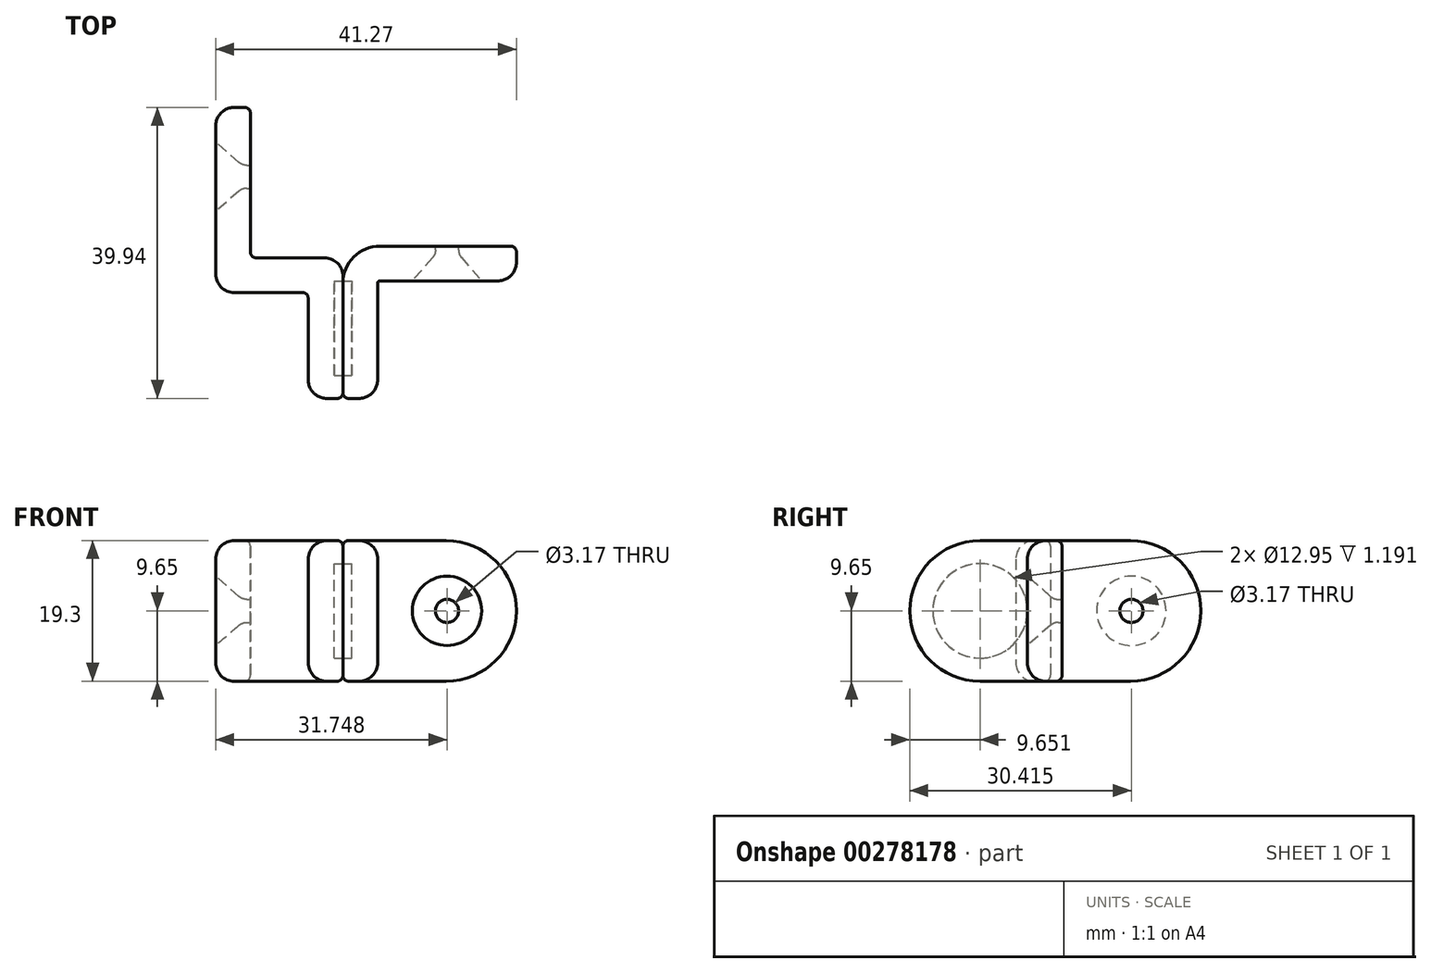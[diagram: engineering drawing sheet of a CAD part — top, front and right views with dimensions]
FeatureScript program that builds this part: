
annotation { "Feature Type Name" : "Feature", "Feature Type Description" : "" }
export const myFeature = defineFeature(function(context is Context, id is Id, definition is map)
    precondition{}
    {
        {
            var Q0;
            Q0=qCreatedBy(makeId("Top.planeOp"),FACE);
            var sketch = newSketch(context, id + "F0", { "sketchPlane" : qUnion([Q0])});
            skLineSegment(sketch, "E0", {"start": v(0, 61) * mm, "end": v(0, 0) * mm, "construction": true});
            skLineSegment(sketch, "E1", {"start": v(0, 0) * mm, "end": v(86.68, 0) * mm, "construction": true});
            skLineSegment(sketch, "E2", {"start": v(0, 19.05) * mm, "end": v(0, -1.59) * mm});
            skLineSegment(sketch, "E3", {"start": v(0, 19.05) * mm, "end": v(-4.76, 19.05) * mm});
            skLineSegment(sketch, "E4", {"start": v(-4.76, 19.05) * mm, "end": v(-4.76, -6.35) * mm});
            skLineSegment(sketch, "E5", {"start": v(0, -1.59) * mm, "end": v(12.7, -1.59) * mm});
            skLineSegment(sketch, "E6", {"start": v(12.7, -1.59) * mm, "end": v(12.7, -20.9) * mm});
            skLineSegment(sketch, "E7", {"start": v(12.7, -20.9) * mm, "end": v(7.94, -20.9) * mm});
            skLineSegment(sketch, "E8", {"start": v(12.7, -4.76) * mm, "end": v(11.5, -4.76) * mm, "construction": true});
            skLineSegment(sketch, "E9", {"start": v(11.5, -4.76) * mm, "end": v(11.5, -17.72) * mm, "construction": true});
            skLineSegment(sketch, "E10", {"start": v(11.5, -17.72) * mm, "end": v(12.7, -17.72) * mm, "construction": true});
            skLineSegment(sketch, "E11", {"start": v(12.7, -11.24) * mm, "end": v(26.67, -11.24) * mm, "construction": true});
            skLineSegment(sketch, "E12", {"start": v(-4.76, 9.53) * mm, "end": v(13.54, 9.53) * mm, "construction": true});
            skLineSegment(sketch, "E13", {"start": v(-4.76, -6.35) * mm, "end": v(7.94, -6.35) * mm});
            skLineSegment(sketch, "E14", {"start": v(7.94, -6.35) * mm, "end": v(7.94, -20.9) * mm});
            skSolve(sketch);
        }
        {
            var Q0;
            Q0=qCreatedBy(makeId("Top.planeOp"),FACE);
            var sketch = newSketch(context, id + "F1", { "sketchPlane" : qUnion([Q0])});
            skLineSegment(sketch, "E15", {"start": v(12.7, 0) * mm, "end": v(12.7, -20.9) * mm});
            skLineSegment(sketch, "E16", {"start": v(12.7, -20.9) * mm, "end": v(17.46, -20.9) * mm});
            skLineSegment(sketch, "E17", {"start": v(17.46, -20.9) * mm, "end": v(17.46, -4.76) * mm});
            skLineSegment(sketch, "E18", {"start": v(17.46, -4.76) * mm, "end": v(36.51, -4.76) * mm});
            skLineSegment(sketch, "E19", {"start": v(36.51, -4.76) * mm, "end": v(36.51, 0) * mm});
            skLineSegment(sketch, "E20", {"start": v(36.51, 0) * mm, "end": v(12.7, 0) * mm});
            skLineSegment(sketch, "E21", {"start": v(11.5, -4.76) * mm, "end": v(12.7, -4.76) * mm, "construction": true});
            skLineSegment(sketch, "E22", {"start": v(11.5, -4.76) * mm, "end": v(11.5, -17.72) * mm, "construction": true});
            skLineSegment(sketch, "E23", {"start": v(12.7, -17.72) * mm, "end": v(11.5, -17.72) * mm, "construction": true});
            skSolve(sketch);
        }
        {
            var Q0;
            Q0 = qSketchRegion(id + "F0", true);
            extrude(context, id + "F2", {"entities" : qUnion([Q0]), "endBound" : BoundingType.SYMMETRIC, "depth" : 19.3 * mm});
        }
        {
            var Q0;
            Q0 = qSketchRegion(id + "F1", true);
            extrude(context, id + "F3", {"entities" : qUnion([Q0]), "endBound" : BoundingType.SYMMETRIC, "depth" : 19.3 * mm});
        }
        {
            var Q0;
            Q0=qCreatedBy(makeId("Top.planeOp"),FACE);
            var sketch = newSketch(context, id + "F4", { "sketchPlane" : qUnion([Q0])});
            skLineSegment(sketch, "E24", {"start": v(12.7, 6.3) * mm, "end": v(12.7, -11.24) * mm, "construction": true});
            skLineSegment(sketch, "E25", {"start": v(12.7, -11.24) * mm, "end": v(26.85, -11.24) * mm, "construction": true});
            skLineSegment(sketch, "E26.bottom", {"start": v(11.5, -4.76) * mm, "end": v(13.9, -4.76) * mm});
            skLineSegment(sketch, "E26.top", {"start": v(11.5, -11.24) * mm, "end": v(13.9, -11.24) * mm});
            skLineSegment(sketch, "E26.left", {"start": v(13.9, -4.76) * mm, "end": v(13.9, -11.24) * mm});
            skLineSegment(sketch, "E26.right", {"start": v(11.5, -4.76) * mm, "end": v(11.5, -11.24) * mm});
            skSolve(sketch);
        }
        {
            var Q0;
            Q0 = qSketchRegion(id + "F4", true);
            var Q1;
            Q1=sQuery(id+"F4.wireOp",EDGE,"E25");
            revolve(context, id + "F5", {"operationType" : NewBodyOperationType.REMOVE, "entities" : qUnion([Q0]), "axis" : qUnion([Q1]), "revolveType" : RevolveType.FULL, "oppositeDirection" : true});
        }
        {
            var Q0;
            Q0=qCreatedBy(makeId("Top.planeOp"),FACE);
            var sketch = newSketch(context, id + "F6", { "sketchPlane" : qUnion([Q0])});
            skLineSegment(sketch, "E27.0", {"start": v(-4.76, 9.53) * mm, "end": v(13.54, 9.53) * mm, "construction": true});
            skLineSegment(sketch, "E28", {"start": v(-4.76, 14.29) * mm, "end": v(-1.11, 11.11) * mm});
            skLineSegment(sketch, "E29", {"start": v(-1.11, 11.11) * mm, "end": v(0, 11.11) * mm});
            skLineSegment(sketch, "E30", {"start": v(0, 11.11) * mm, "end": v(0, 9.53) * mm});
            skLineSegment(sketch, "E31", {"start": v(0, 9.53) * mm, "end": v(-4.76, 9.53) * mm});
            skLineSegment(sketch, "E32", {"start": v(-4.76, 14.29) * mm, "end": v(-4.76, 9.53) * mm});
            skSolve(sketch);
        }
        {
            var Q0;
            Q0 = qSketchRegion(id + "F6", true);
            var Q1;
            Q1=sQuery(id+"F6.wireOp",EDGE,"E27.0");
            revolve(context, id + "F7", {"operationType" : NewBodyOperationType.REMOVE, "entities" : qUnion([Q0]), "axis" : qUnion([Q1]), "revolveType" : RevolveType.FULL, "oppositeDirection" : true});
        }
        {
            var Q0;
            Q0=qCreatedBy(makeId("Top.planeOp"),FACE);
            var sketch = newSketch(context, id + "F8", { "sketchPlane" : qUnion([Q0])});
            skLineSegment(sketch, "E33", {"start": v(26.99, -4.76) * mm, "end": v(26.99, 16.5) * mm, "construction": true});
            skLineSegment(sketch, "E34", {"start": v(28.58, 0) * mm, "end": v(28.58, -1.11) * mm});
            skLineSegment(sketch, "E35", {"start": v(28.58, -1.11) * mm, "end": v(31.75, -4.76) * mm});
            skLineSegment(sketch, "E36", {"start": v(31.75, -4.76) * mm, "end": v(26.99, -4.76) * mm});
            skLineSegment(sketch, "E37", {"start": v(26.99, -4.76) * mm, "end": v(26.99, 0) * mm});
            skLineSegment(sketch, "E38", {"start": v(26.99, 0) * mm, "end": v(28.58, 0) * mm});
            skSolve(sketch);
        }
        {
            var Q0;
            Q0 = qSketchRegion(id + "F8", true);
            var Q1;
            Q1=sQuery(id+"F8.wireOp",EDGE,"E33");
            revolve(context, id + "F9", {"operationType" : NewBodyOperationType.REMOVE, "entities" : qUnion([Q0]), "axis" : qUnion([Q1]), "revolveType" : RevolveType.FULL, "oppositeDirection" : true});
        }
        {
            var Q0;
            Q0=makeQuery(id+"F2.opExtrude","CAP_EDGE",EDGE,{"disambiguationData":[OSD([sQuery(id+"F0.wireOp",EDGE,"E7")])],"isStart":false});
            var Q1;
            Q1=makeQuery(id+"F3.opExtrude","CAP_EDGE",EDGE,{"disambiguationData":[OSD([sQuery(id+"F1.wireOp",EDGE,"E16")])],"isStart":false});
            var Q2;
            Q2=makeQuery(id+"F3.opExtrude","CAP_EDGE",EDGE,{"disambiguationData":[OSD([sQuery(id+"F1.wireOp",EDGE,"E16")])],"isStart":true});
            var Q3;
            Q3=makeQuery(id+"F2.opExtrude","CAP_EDGE",EDGE,{"disambiguationData":[OSD([sQuery(id+"F0.wireOp",EDGE,"E7")])],"isStart":true});
            fillet(context, id + "F10", {"entities" : qUnion([Q0, Q1, Q2, Q3]), "radius" : 9.65 * mm, "tangentPropagation" : true, "allowEdgeOverflow" : false});
        }
        {
            var Q0;
            Q0=makeQuery(id+"F2.opExtrude","CAP_EDGE",EDGE,{"disambiguationData":[OSD([sQuery(id+"F0.wireOp",EDGE,"E3")])],"isStart":false});
            var Q1;
            Q1=makeQuery(id+"F2.opExtrude","CAP_EDGE",EDGE,{"disambiguationData":[OSD([sQuery(id+"F0.wireOp",EDGE,"E3")])],"isStart":true});
            var Q2;
            Q2=makeQuery(id+"F3.opExtrude","CAP_EDGE",EDGE,{"disambiguationData":[OSD([sQuery(id+"F1.wireOp",EDGE,"E19")])],"isStart":false});
            var Q3;
            Q3=makeQuery(id+"F3.opExtrude","CAP_EDGE",EDGE,{"disambiguationData":[OSD([sQuery(id+"F1.wireOp",EDGE,"E19")])],"isStart":true});
            fillet(context, id + "F11", {"entities" : qUnion([Q0, Q1, Q2, Q3]), "radius" : 9.65 * mm, "tangentPropagation" : true, "allowEdgeOverflow" : false});
        }
        {
            var Q0;
            Q0=makeQuery(id+"F3.opExtrude","SWEPT_EDGE",EDGE,{"disambiguationData":[OSD([sQuery(id+"F1.wireOp",EDGE,"E15"),sQuery(id+"F1.wireOp",EDGE,"E20")])]});
            fillet(context, id + "F12", {"entities" : qUnion([Q0]), "radius" : 5.08 * mm, "tangentPropagation" : true, "allowEdgeOverflow" : false});
        }
        {
            var Q0;
            Q0=makeQuery(id+"F3.opExtrude","SWEPT_EDGE",EDGE,{"disambiguationData":[OSD([sQuery(id+"F1.wireOp",EDGE,"E17"),sQuery(id+"F1.wireOp",EDGE,"E18")])]});
            fillet(context, id + "F13", {"entities" : qUnion([Q0]), "radius" : 0.32 * mm, "tangentPropagation" : true, "allowEdgeOverflow" : false});
        }
        {
            var Q0;
            Q0=makeQuery(id+"F2.opExtrude","SWEPT_EDGE",EDGE,{"disambiguationData":[OSD([sQuery(id+"F0.wireOp",EDGE,"E5"),sQuery(id+"F0.wireOp",EDGE,"E6")])]});
            fillet(context, id + "F14", {"entities" : qUnion([Q0]), "radius" : 2.54 * mm, "tangentPropagation" : true, "allowEdgeOverflow" : false});
        }
        {
            var Q0;
            Q0=makeQuery(id+"F2.opExtrude","CAP_EDGE",EDGE,{"disambiguationData":[OSD([sQuery(id+"F0.wireOp",EDGE,"E4")])],"isStart":false});
            var Q1;
            Q1=makeQuery(id+"F3.opExtrude","CAP_EDGE",EDGE,{"disambiguationData":[OSD([sQuery(id+"F1.wireOp",EDGE,"E18")])],"isStart":false});
            fillet(context, id + "F15", {"entities" : qUnion([Q0, Q1]), "radius" : 2.54 * mm, "tangentPropagation" : true, "allowEdgeOverflow" : false});
        }
        {
            var Q0;
            Q0=makeQuery(id+"F2.opExtrude","SWEPT_EDGE",EDGE,{"disambiguationData":[OSD([sQuery(id+"F0.wireOp",EDGE,"E2"),sQuery(id+"F0.wireOp",EDGE,"E5")])]});
            var Q1;
            Q1=makeQuery(id+"F2.opExtrude","SWEPT_EDGE",EDGE,{"disambiguationData":[OSD([sQuery(id+"F0.wireOp",EDGE,"E13"),sQuery(id+"F0.wireOp",EDGE,"E14")])]});
            fillet(context, id + "F16", {"entities" : qUnion([Q0, Q1]), "radius" : 0.8 * mm, "tangentPropagation" : true, "allowEdgeOverflow" : false});
        }
        {
            var Q0;
            Q0=makeQuery(id+"F2.opExtrude","CAP_EDGE",EDGE,{"disambiguationData":[OSD([sQuery(id+"F0.wireOp",EDGE,"E2")])],"isStart":false});
            var Q1;
            Q1=makeQuery(id+"F3.opExtrude","CAP_EDGE",EDGE,{"disambiguationData":[OSD([sQuery(id+"F1.wireOp",EDGE,"E20")])],"isStart":false});
            fillet(context, id + "F17", {"entities" : qUnion([Q0, Q1]), "radius" : 0.8 * mm, "tangentPropagation" : true, "allowEdgeOverflow" : false});
        }
        {
            var Q0;
            Q0=makeQuery(id+"F7.boolean.opBoolean","COPY",EDGE,{"derivedFrom":makeQuery(id+"F7.opRevolve","SWEPT_EDGE",EDGE,{"disambiguationData":[OSD([sQuery(id+"F6.wireOp",EDGE,"E28"),sQuery(id+"F6.wireOp",EDGE,"E32")])]})});
            var Q1;
            Q1=makeQuery(id+"F9.boolean.opBoolean","COPY",EDGE,{"derivedFrom":makeQuery(id+"F9.opRevolve","SWEPT_EDGE",EDGE,{"disambiguationData":[OSD([sQuery(id+"F8.wireOp",EDGE,"E35"),sQuery(id+"F8.wireOp",EDGE,"E36")])]})});
            var Q2;
            Q2=makeQuery(id+"F9.boolean.opBoolean","COPY",EDGE,{"derivedFrom":makeQuery(id+"F9.opRevolve","SWEPT_EDGE",EDGE,{"disambiguationData":[OSD([sQuery(id+"F8.wireOp",EDGE,"E34"),sQuery(id+"F8.wireOp",EDGE,"E35")])]})});
            var Q3;
            Q3=makeQuery(id+"F7.boolean.opBoolean","COPY",EDGE,{"derivedFrom":makeQuery(id+"F7.opRevolve","SWEPT_EDGE",EDGE,{"disambiguationData":[OSD([sQuery(id+"F6.wireOp",EDGE,"E28"),sQuery(id+"F6.wireOp",EDGE,"E29")])]})});
            fillet(context, id + "F18", {"entities" : qUnion([Q0, Q1, Q2, Q3]), "radius" : 1.59 * mm, "tangentPropagation" : true, "allowEdgeOverflow" : false});
        }
        {
            var Q0;
            Q0=makeQuery(id+"F2.opExtrude","CAP_EDGE",EDGE,{"disambiguationData":[OSD([sQuery(id+"F0.wireOp",EDGE,"E13")])],"isStart":false});
            fillet(context, id + "F19", {"entities" : qUnion([Q0]), "radius" : 2.54 * mm, "tangentPropagation" : true, "allowEdgeOverflow" : false});
        }
    });
